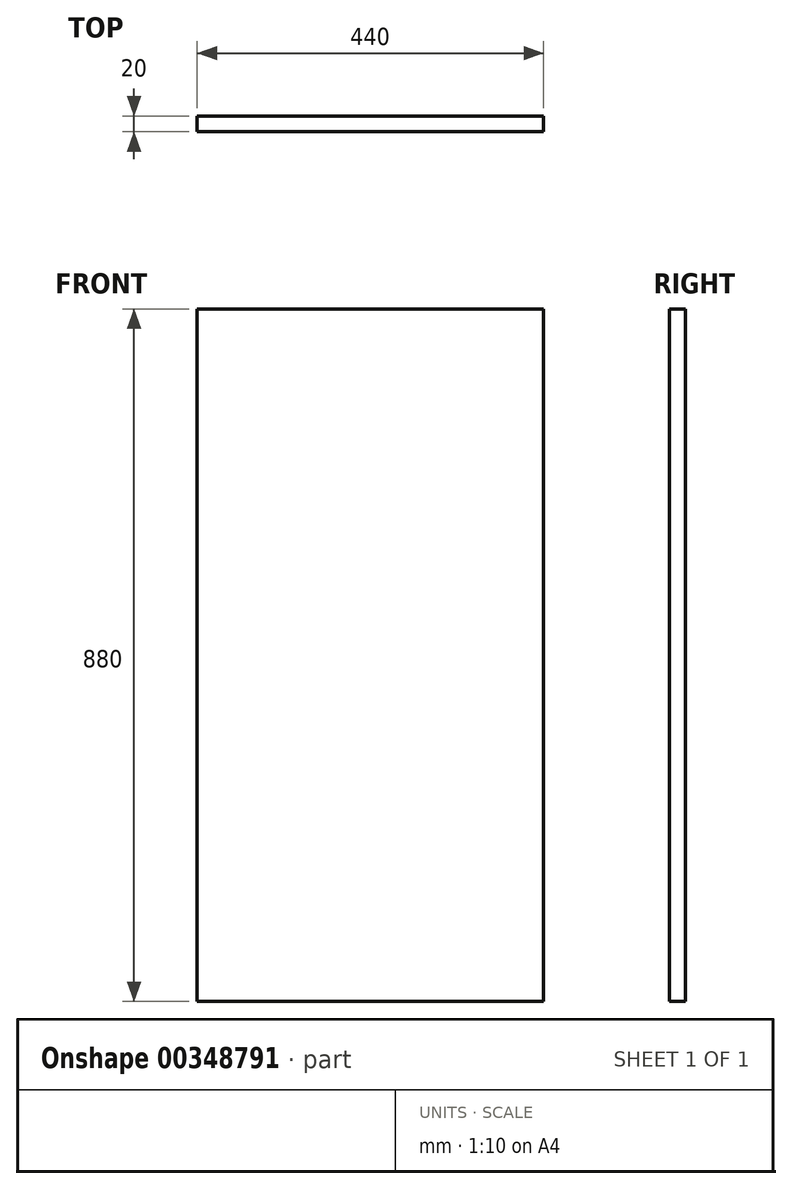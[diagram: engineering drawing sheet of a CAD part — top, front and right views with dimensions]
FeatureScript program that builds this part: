
annotation { "Feature Type Name" : "Feature", "Feature Type Description" : "" }
export const myFeature = defineFeature(function(context is Context, id is Id, definition is map)
    precondition{}
    {
        {
            var Q0;
            Q0=qCreatedBy(makeId("Front.planeOp"),FACE);
            var sketch = newSketch(context, id + "F0", { "sketchPlane" : qUnion([Q0])});
            skLineSegment(sketch, "E0.bottom", {"start": v(-440, -880) * mm, "end": v(0, -880) * mm});
            skLineSegment(sketch, "E0.top", {"start": v(-440, 0) * mm, "end": v(0, 0) * mm});
            skLineSegment(sketch, "E0.left", {"start": v(-440, -880) * mm, "end": v(-440, 0) * mm});
            skLineSegment(sketch, "E0.right", {"start": v(0, -880) * mm, "end": v(0, 0) * mm});
            skSolve(sketch);
        }
        {
            var Q0;
            Q0=qSketchRegion(id+"F0",true);
            extrude(context, id + "F1", {"entities" : qUnion([Q0]), "depth" : 20 * mm});
        }
    });
